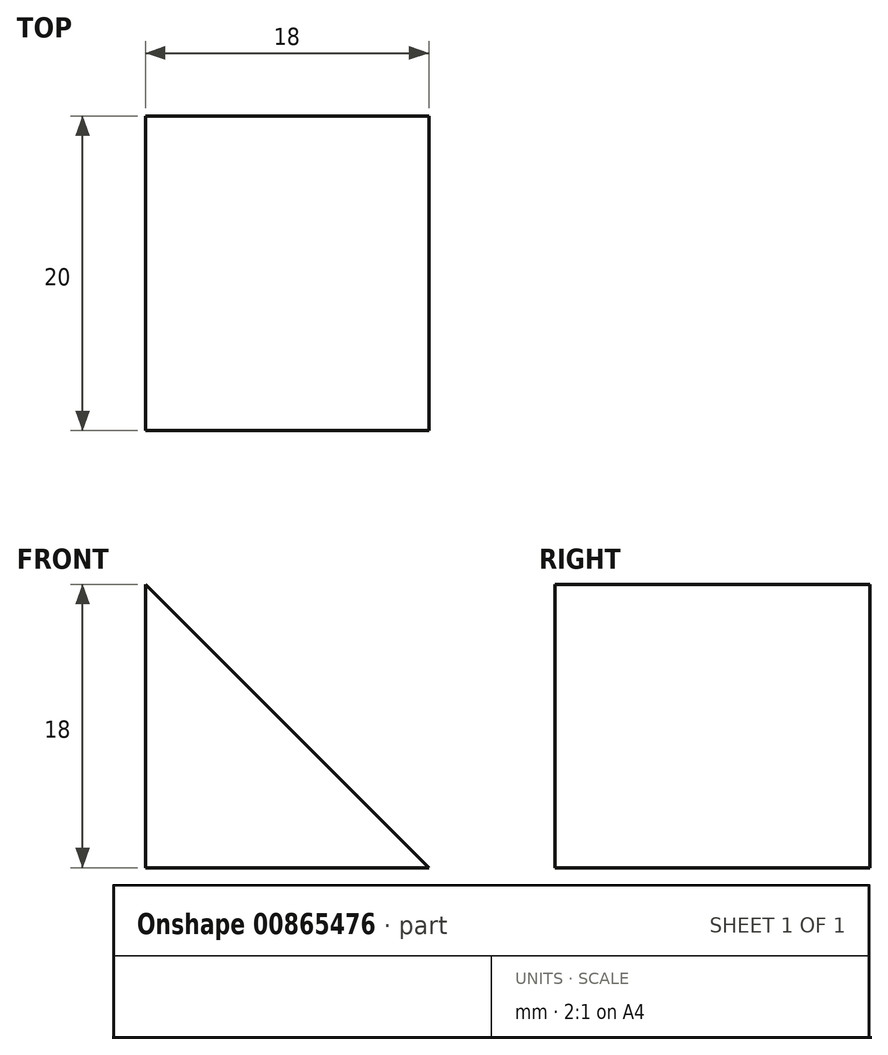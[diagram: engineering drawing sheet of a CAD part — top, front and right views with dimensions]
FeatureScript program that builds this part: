
annotation { "Feature Type Name" : "Feature", "Feature Type Description" : "" }
export const myFeature = defineFeature(function(context is Context, id is Id, definition is map)
    precondition{}
    {
        {
            var Q0;
            Q0=qCreatedBy(makeId("Front.planeOp"),FACE);
            var sketch = newSketch(context, id + "F0", { "sketchPlane" : qUnion([Q0])});
            skLineSegment(sketch, "E0", {"start": v(0, 0) * mm, "end": v(0, 18) * mm});
            skLineSegment(sketch, "E1", {"start": v(0, 18) * mm, "end": v(18, 0) * mm});
            skLineSegment(sketch, "E2", {"start": v(18, 0) * mm, "end": v(0, 0) * mm});
            skSolve(sketch);
        }
        {
            var Q0;
            Q0 = qSketchRegion(id + "F0", true);
            extrude(context, id + "F1", {"entities" : qUnion([Q0]), "depth" : 20 * mm, "offsetDistance" : 25 * mm});
        }
    });
